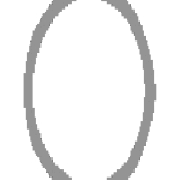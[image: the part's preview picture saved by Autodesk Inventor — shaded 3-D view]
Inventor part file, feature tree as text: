
AUTODESK INVENTOR PART (.ipt)
format: ipt  version: 2021 (Build 250183000, 183)  size: 113,152 bytes
history: native  units: in
note: dims shown in document units (in); Inventor stores cm internally (conversion verified against a paired STEP export)
features: other x4, sketch x3, plane x1
ambient origin geometry x8: Origin, YZ Plane, XZ Plane, XY Plane, X Axis, Y Axis, Z Axis, Center Point
bodies: Solid1 (feature_tree), Body (feature_tree)
feature tree (8):
  other  "Driven Length"
  other  "Frame Generator"
  other  "Start Plane"
  other  "End Plane"
  sketch  "Sketch"  dims[d2=3.0in d4=-0.0in d5=3.0in d6=0.12in d7=0.0in d8=90.0deg d9=3.0in]
  sketch  "Sketch2"  dims[d0=1.0in]
  plane  "Work Plane3"
  sketch  "Sketch3"  dims[d1=0.065in]
